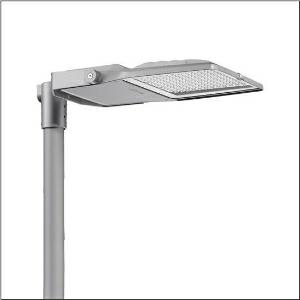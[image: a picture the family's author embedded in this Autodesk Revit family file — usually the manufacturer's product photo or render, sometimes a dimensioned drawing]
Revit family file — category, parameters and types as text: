
# Revit family: floodlight_fl_21_iq_midi___pl64_5xa7781e4e3a_69c6
name_source: partatom
category: Lighting Fixtures
units: mm (PartAtom-declared; Revit-internal decimal feet)

## family parameters
Cut with Voids When Loaded = No
Host = Face
Light Source = No
Part Type = Normal
Room Calculation Point = No
Round Connector Dimension = Use Diameter
Shared = No

## types (1)
- --- (1 x LED, 27050 lm, 208.1 W, 4000K)
    Apparent Load = 208 VA
    CIE Flux Codes = 28 80 98 100 100
    Color Rendering = 70
    Color Temperature = 4000K
    Default Elevation = 1800 mm
    Description = Floodlight FL 21 iQ midi, floodlight, primary light control with lens, of PMMA, primary optical cover: protective disc, of toughened safety glass, transparent, light distribution: PL64, light emission: direct distribution, installation type: surface-mounted, LED, High Power LED, rated luminous flux: 27.050lm, luminous efficacy: 130lm/W, light colour: 740, colour temperature: 4000K, control gear: iQ Comfort/DALI, control: optimised constant luminous flux control (CLO 2.0), Desk-Remote (wireless, voltage-free reading and setting of iQ features in the workshop via application-optimized NFC function/RFID function), Light-Fading, Smart-Wire, Night-Set, Lumen-Switch, Temp-Guard, Auto-Match, with terminal, 6-pole, mains connection: 220..240V, AC, 50/60Hz, start of lifetime: 208W, end of service life: 227W, reduction: 90W, luminaire housing, of diecast aluminium, powder-coated, Siteco® metallic grey (DB 702S), corrosivity category C5 mid according to DIN EN ISO 12944, suitable for swimming pools, chlorine-resistant, sealing non-destructively replaceable, please order mast flange separately, mast bracket, of steel, galvanised, powder-coated, Siteco® metallic grey (DB 702S), protection rating (complete): IP66, insulation class (complete): insulation class II (safety insulation), certification: CE, ENEC, VDE, protection symbol: D, impact resistance: IK08, permissible operating ambient temperature: -40..+40°C, permissible operating ambient temperature for outdoor applications: -40..+50°C, standard: DIN EN 12944, LABS conformity tested according to VDMA 24364:2018-05, packaging unit: 1 piece

Light Distribution: PL64
    Height = 76 mm
    Lamp = 1 x LED
    Lamp Light Flux = 27050 lm
    Lamp Power = 208.1 W
    Lamp count = 1
    Length = 657 mm
    Luminous efficacy = 130 lm/W
    Manufacturer = Siteco
    ModVariant = No
    Model = 5XA7781E4E3A
    Number of Poles = 1
    OnlyDefault = Yes
    Power Factor = 1
    Product Name = Floodlight FL 21 iQ midi | PL64
    Product group = floodlight | pylon annexe
    ProductGroupID = 6200
    Protection Class = Protection class II
    Protection Degree = IP 66
    RLX_Detail_Level = 1
    RLX_Emergency_Light_Flux = 0 lm
    RLX_Emergency_Type = 0
    RLX_Emergency_Type_DB = No
    RlxData = <blob elided: 153569 chars, md5=f16057ec>
    Socket = socket
    Standby Power = 0 W
    System Light Flux = 27050 lm
    System Power = 208 W
    Type Comments = factory setting: luminous flux: 100 % | dim-lin: 254 | 710 mA
    Type Image = l_1007123.jpg
    URL = http://relux.com
    VarID = @adj_107210
    Voltage = 0 V
    Weight = 0.00 kg
    Width = 442 mm

## geometry (parser evidence)
native form markers: Blend x4, Sweep x12
no freeform markers — native parametric forms only
